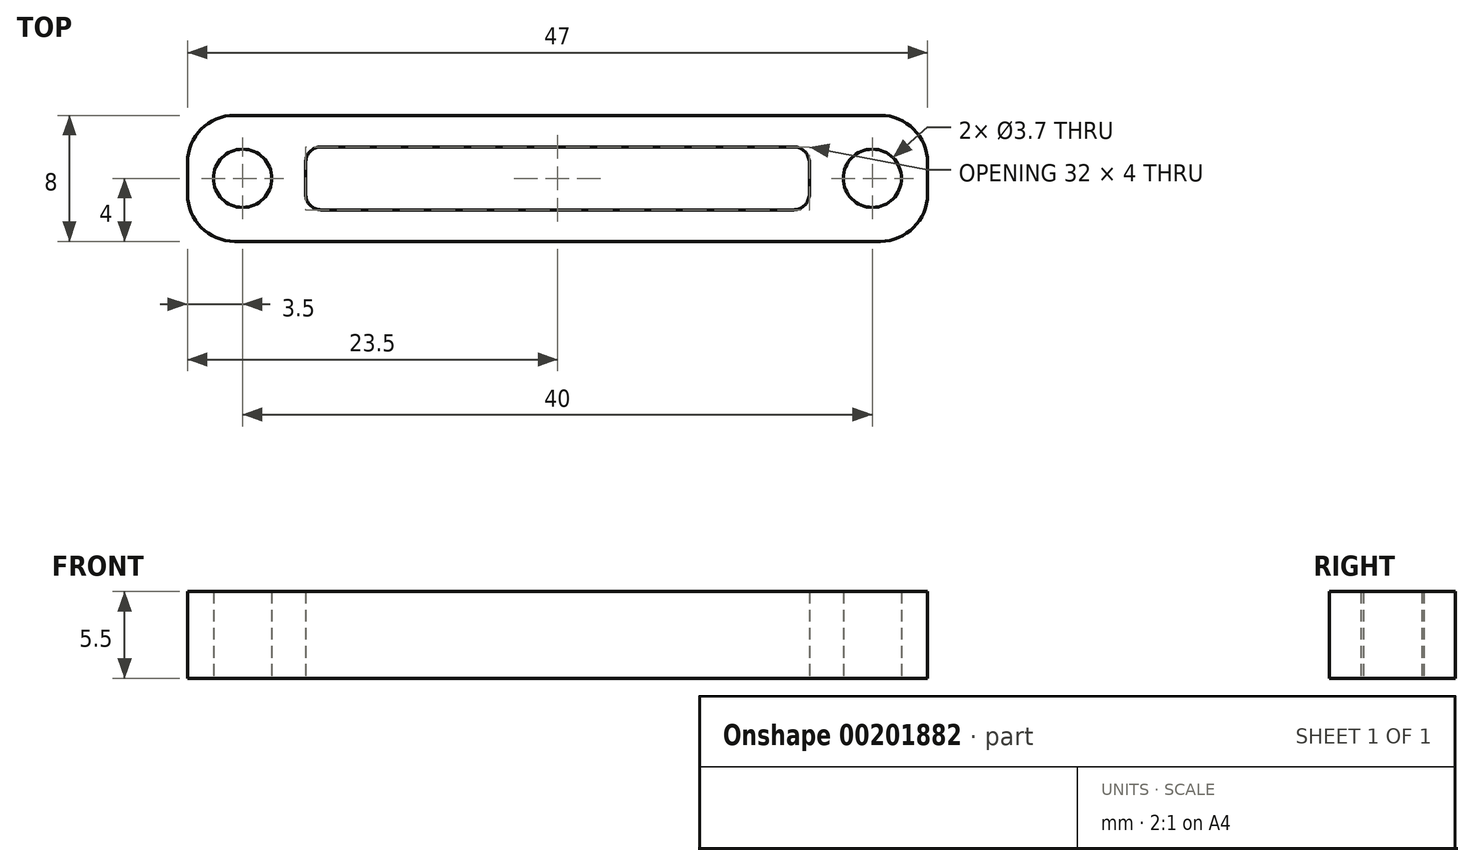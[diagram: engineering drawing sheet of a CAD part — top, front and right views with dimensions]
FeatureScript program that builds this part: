
annotation { "Feature Type Name" : "Feature", "Feature Type Description" : "" }
export const myFeature = defineFeature(function(context is Context, id is Id, definition is map)
    precondition{}
    {
        {
            var Q0;
            Q0=qCreatedBy(makeId("Top.planeOp"),FACE);
            var sketch = newSketch(context, id + "F0", { "sketchPlane" : qUnion([Q0])});
            skLineSegment(sketch, "E0.bottom", {"start": v(23.5, 4) * mm, "end": v(-23.5, 4) * mm});
            skLineSegment(sketch, "E0.top", {"start": v(23.5, -4) * mm, "end": v(-23.5, -4) * mm});
            skLineSegment(sketch, "E0.left", {"start": v(23.5, 4) * mm, "end": v(23.5, -4) * mm});
            skLineSegment(sketch, "E0.right", {"start": v(-23.5, 4) * mm, "end": v(-23.5, -4) * mm});
            skPoint(sketch, "E0.middle", {"position": v(0, 0) * mm});
            skCircle(sketch, "E1", {"center": v(-20, 0) * mm, "radius": 1.85 * mm});
            skCircle(sketch, "E2", {"center": v(20, 0) * mm, "radius": 1.85 * mm});
            skPoint(sketch, "E2.centerSnap0", {"position": v(23.5, 0) * mm});
            skLineSegment(sketch, "E3.bottom", {"start": v(16, 2) * mm, "end": v(-16, 2) * mm});
            skLineSegment(sketch, "E3.top", {"start": v(16, -2) * mm, "end": v(-16, -2) * mm});
            skLineSegment(sketch, "E3.left", {"start": v(16, 2) * mm, "end": v(16, -2) * mm});
            skLineSegment(sketch, "E3.right", {"start": v(-16, 2) * mm, "end": v(-16, -2) * mm});
            skSolve(sketch);
        }
        {
            var Q0;
            Q0=makeQuery(id+"F0.imprint","IMPRINT",FACE,{"disambiguationData":[TD([[makeQuery(id+"F0.imprint","IMPRINT",EDGE,{"derivedFrom":sQuery(id+"F0.wireOp",EDGE,"E0.bottom")}),1.0]])]});
            extrude(context, id + "F1", {"entities" : qUnion([Q0]), "depth" : 5.5 * mm});
        }
        {
            var Q0;
            Q0=makeQuery(id+"F1.opExtrude","SWEPT_EDGE",EDGE,{"disambiguationData":[OSD([sQuery(id+"F0.wireOp",EDGE,"E0.top"),sQuery(id+"F0.wireOp",EDGE,"E0.left")])]});
            var Q1;
            Q1=makeQuery(id+"F1.opExtrude","SWEPT_EDGE",EDGE,{"disambiguationData":[OSD([sQuery(id+"F0.wireOp",EDGE,"E0.bottom"),sQuery(id+"F0.wireOp",EDGE,"E0.left")])]});
            var Q2;
            Q2=makeQuery(id+"F1.opExtrude","SWEPT_EDGE",EDGE,{"disambiguationData":[OSD([sQuery(id+"F0.wireOp",EDGE,"E0.top"),sQuery(id+"F0.wireOp",EDGE,"E0.right")])]});
            var Q3;
            Q3=makeQuery(id+"F1.opExtrude","SWEPT_EDGE",EDGE,{"disambiguationData":[OSD([sQuery(id+"F0.wireOp",EDGE,"E0.bottom"),sQuery(id+"F0.wireOp",EDGE,"E0.right")])]});
            fillet(context, id + "F2", {"entities" : qUnion([Q0, Q1, Q2, Q3]), "radius" : 3 * mm, "tangentPropagation" : true, "allowEdgeOverflow" : false});
        }
        {
            var Q0;
            Q0=makeQuery(id+"F1.opExtrude","SWEPT_EDGE",EDGE,{"disambiguationData":[OSD([sQuery(id+"F0.wireOp",EDGE,"E3.bottom"),sQuery(id+"F0.wireOp",EDGE,"E3.right")])]});
            var Q1;
            Q1=makeQuery(id+"F1.opExtrude","SWEPT_EDGE",EDGE,{"disambiguationData":[OSD([sQuery(id+"F0.wireOp",EDGE,"E3.bottom"),sQuery(id+"F0.wireOp",EDGE,"E3.left")])]});
            var Q2;
            Q2=makeQuery(id+"F1.opExtrude","SWEPT_EDGE",EDGE,{"disambiguationData":[OSD([sQuery(id+"F0.wireOp",EDGE,"E3.top"),sQuery(id+"F0.wireOp",EDGE,"E3.left")])]});
            var Q3;
            Q3=makeQuery(id+"F1.opExtrude","SWEPT_EDGE",EDGE,{"disambiguationData":[OSD([sQuery(id+"F0.wireOp",EDGE,"E3.top"),sQuery(id+"F0.wireOp",EDGE,"E3.right")])]});
            fillet(context, id + "F3", {"entities" : qUnion([Q0, Q1, Q2, Q3]), "radius" : 1 * mm, "tangentPropagation" : true, "allowEdgeOverflow" : false});
        }
    });
